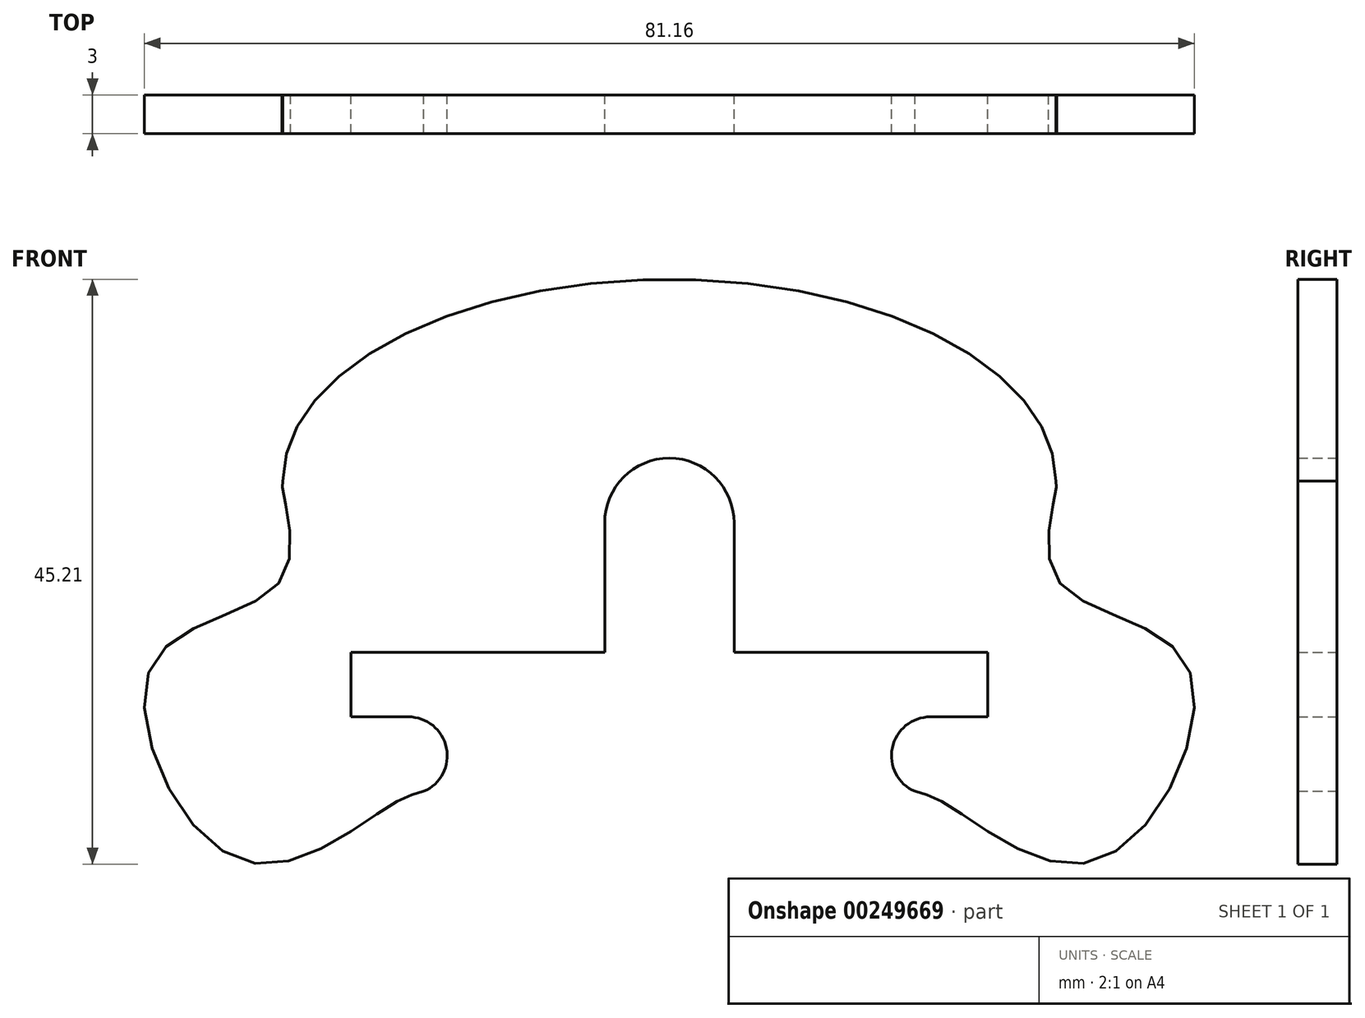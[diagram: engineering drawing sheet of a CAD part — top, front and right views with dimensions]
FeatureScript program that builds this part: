
annotation { "Feature Type Name" : "Feature", "Feature Type Description" : "" }
export const myFeature = defineFeature(function(context is Context, id is Id, definition is map)
    precondition{}
    {
        {
            var Q0;
            Q0=qCreatedBy(makeId("Front.planeOp"),FACE);
            var sketch = newSketch(context, id + "F0", { "sketchPlane" : qUnion([Q0])});
            skLineSegment(sketch, "E0", {"start": v(-24.6, -12.8) * mm, "end": v(-24.6, -7.8) * mm});
            skLineSegment(sketch, "E1", {"start": v(24.6, -12.8) * mm, "end": v(24.6, -7.8) * mm});
            skLineSegment(sketch, "E2", {"start": v(-24.6, -7.8) * mm, "end": v(-5, -7.8) * mm});
            skLineSegment(sketch, "E3", {"start": v(5, -7.8) * mm, "end": v(24.6, -7.8) * mm});
            skLineSegment(sketch, "E4", {"start": v(-24.6, -12.8) * mm, "end": v(-20.17, -12.8) * mm});
            skFitSpline(sketch, "E5", {"points": [v(-29.87, 5.43) * mm, v(-29.92, 4.95) * mm, v(-29.94, -2.15) * mm, v(-40.01, -8.83) * mm, v(-33.12, -23.88) * mm, v(-21.73, -19.75) * mm, v(-18.98, -18.56) * mm]});
            skArc(sketch, "E6", {"start": v(-18.98, -18.56) * mm, "mid": v(-17.23, -15.2) * mm, "end": v(-20.17, -12.8) * mm});
            skLineSegment(sketch, "E7", {"start": v(24.6, -12.8) * mm, "end": v(20.17, -12.8) * mm});
            skFitSpline(sketch, "E8", {"points": [v(29.87, 5.43) * mm, v(29.92, 4.95) * mm, v(29.94, -2.15) * mm, v(40.01, -8.83) * mm, v(33.12, -23.88) * mm, v(21.73, -19.75) * mm, v(18.98, -18.56) * mm]});
            skArc(sketch, "E9", {"start": v(20.17, -12.8) * mm, "mid": v(17.23, -15.2) * mm, "end": v(18.98, -18.56) * mm});
            skEllipticalArc(sketch, "E10", {});
            skLineSegment(sketch, "E11", {"start": v(5, -7.8) * mm, "end": v(5, 2.2) * mm});
            skLineSegment(sketch, "E12", {"start": v(-5, -7.8) * mm, "end": v(-5, 2.2) * mm});
            skArc(sketch, "E13", {"start": v(5, 2.2) * mm, "mid": v(0, 7.2) * mm, "end": v(-5, 2.2) * mm});
            const initialGuessF0  = {"E10": [0, 0.005432538000000022, 29.869969, 0, 0.029869969000000003, 0.015588385000000001, 0, 3.141593]};
            skSetInitialGuess(sketch, initialGuessF0);
            skSolve(sketch);
        }
        {
            var Q0;
            Q0=makeQuery(id+"F0.imprint","IMPRINT",FACE,{"disambiguationData":[TD([[makeQuery(id+"F0.imprint","IMPRINT",EDGE,{"derivedFrom":sQuery(id+"F0.wireOp",EDGE,"E0")}),1.0]])]});
            extrude(context, id + "F1", {"entities" : qUnion([Q0]), "depth" : 3 * mm});
        }
    });
